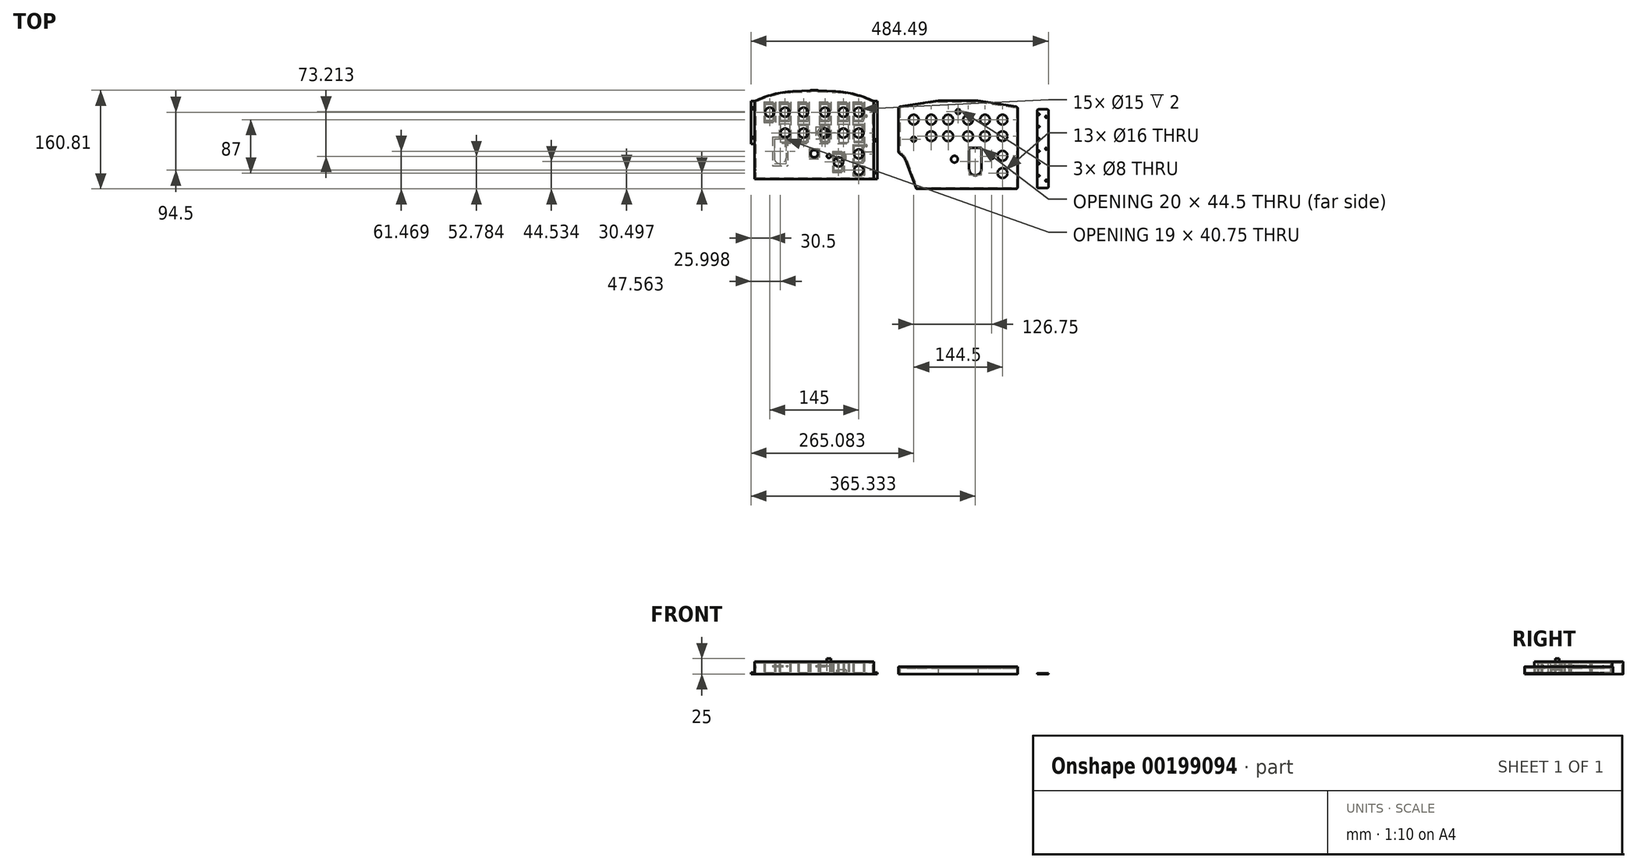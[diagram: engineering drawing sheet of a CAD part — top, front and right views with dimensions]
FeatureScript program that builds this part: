
annotation { "Feature Type Name" : "Feature", "Feature Type Description" : "" }
export const myFeature = defineFeature(function(context is Context, id is Id, definition is map)
    precondition{}
    {
        {
            var Q0;
            Q0=qCreatedBy(makeId("Top.planeOp"),FACE);
            var sketch = newSketch(context, id + "F0", { "sketchPlane" : qUnion([Q0])});
            skLineSegment(sketch, "E0.bottom", {"start": v(-74, 30.66) * mm, "end": v(-59, 30.66) * mm});
            skLineSegment(sketch, "E0.top", {"start": v(-74, 0.66) * mm, "end": v(-59, 0.66) * mm});
            skLineSegment(sketch, "E0.left", {"start": v(-74, 30.66) * mm, "end": v(-74, 0.66) * mm});
            skLineSegment(sketch, "E0.right", {"start": v(-59, 30.66) * mm, "end": v(-59, 0.66) * mm});
            skLineSegment(sketch, "E1.bottom", {"start": v(-49, 30.66) * mm, "end": v(-34, 30.66) * mm});
            skLineSegment(sketch, "E1.top", {"start": v(-49, 0.66) * mm, "end": v(-34, 0.66) * mm});
            skLineSegment(sketch, "E1.left", {"start": v(-49, 30.66) * mm, "end": v(-49, 0.66) * mm});
            skLineSegment(sketch, "E1.right", {"start": v(-34, 30.66) * mm, "end": v(-34, 0.66) * mm});
            skLineSegment(sketch, "E2.bottom", {"start": v(-19, 30.66) * mm, "end": v(-4, 30.66) * mm});
            skLineSegment(sketch, "E2.top", {"start": v(-19, 0.66) * mm, "end": v(-4, 0.66) * mm});
            skLineSegment(sketch, "E2.left", {"start": v(-19, 30.66) * mm, "end": v(-19, 0.66) * mm});
            skLineSegment(sketch, "E2.right", {"start": v(-4, 30.66) * mm, "end": v(-4, 0.66) * mm});
            skLineSegment(sketch, "E3.bottom", {"start": v(16, 30.66) * mm, "end": v(31, 30.66) * mm});
            skLineSegment(sketch, "E3.top", {"start": v(16, 0.66) * mm, "end": v(31, 0.66) * mm});
            skLineSegment(sketch, "E3.left", {"start": v(16, 30.66) * mm, "end": v(16, 0.66) * mm});
            skLineSegment(sketch, "E3.right", {"start": v(31, 30.66) * mm, "end": v(31, 0.66) * mm});
            skLineSegment(sketch, "E4.bottom", {"start": v(46, 30.66) * mm, "end": v(61, 30.66) * mm});
            skLineSegment(sketch, "E4.top", {"start": v(46, 0.66) * mm, "end": v(61, 0.66) * mm});
            skLineSegment(sketch, "E4.left", {"start": v(46, 30.66) * mm, "end": v(46, 0.66) * mm});
            skLineSegment(sketch, "E4.right", {"start": v(61, 30.66) * mm, "end": v(61, 0.66) * mm});
            skLineSegment(sketch, "E5.bottom", {"start": v(71, 30.66) * mm, "end": v(86, 30.66) * mm});
            skLineSegment(sketch, "E5.top", {"start": v(71, 0.66) * mm, "end": v(86, 0.66) * mm});
            skLineSegment(sketch, "E5.left", {"start": v(71, 30.66) * mm, "end": v(71, 0.66) * mm});
            skLineSegment(sketch, "E5.right", {"start": v(86, 30.66) * mm, "end": v(86, 0.66) * mm});
            skLineSegment(sketch, "E6.bottom", {"start": v(-19, -3.34) * mm, "end": v(-4, -3.34) * mm});
            skLineSegment(sketch, "E6.top", {"start": v(-19, -33.34) * mm, "end": v(-4, -33.34) * mm});
            skLineSegment(sketch, "E6.left", {"start": v(-19, -3.34) * mm, "end": v(-19, -33.34) * mm});
            skLineSegment(sketch, "E6.right", {"start": v(-4, -3.34) * mm, "end": v(-4, -33.34) * mm});
            skLineSegment(sketch, "E7.bottom", {"start": v(16, -3.34) * mm, "end": v(31, -3.34) * mm});
            skLineSegment(sketch, "E7.top", {"start": v(16, -33.34) * mm, "end": v(31, -33.34) * mm});
            skLineSegment(sketch, "E7.left", {"start": v(16, -3.34) * mm, "end": v(16, -33.34) * mm});
            skLineSegment(sketch, "E7.right", {"start": v(31, -3.34) * mm, "end": v(31, -33.34) * mm});
            skLineSegment(sketch, "E8.bottom", {"start": v(46, -3.34) * mm, "end": v(61, -3.34) * mm});
            skLineSegment(sketch, "E8.top", {"start": v(46, -33.34) * mm, "end": v(61, -33.34) * mm});
            skLineSegment(sketch, "E8.left", {"start": v(46, -3.34) * mm, "end": v(46, -33.34) * mm});
            skLineSegment(sketch, "E8.right", {"start": v(61, -3.34) * mm, "end": v(61, -33.34) * mm});
            skLineSegment(sketch, "E9.bottom", {"start": v(71, -3.34) * mm, "end": v(86, -3.34) * mm});
            skLineSegment(sketch, "E9.top", {"start": v(71, -33.34) * mm, "end": v(86, -33.34) * mm});
            skLineSegment(sketch, "E9.left", {"start": v(71, -3.34) * mm, "end": v(71, -33.34) * mm});
            skLineSegment(sketch, "E9.right", {"start": v(86, -3.34) * mm, "end": v(86, -33.34) * mm});
            skLineSegment(sketch, "E10.bottom", {"start": v(71, -37.34) * mm, "end": v(86, -37.34) * mm});
            skLineSegment(sketch, "E10.top", {"start": v(71, -67.34) * mm, "end": v(86, -67.34) * mm});
            skLineSegment(sketch, "E10.left", {"start": v(71, -37.34) * mm, "end": v(71, -67.34) * mm});
            skLineSegment(sketch, "E10.right", {"start": v(86, -37.34) * mm, "end": v(86, -67.34) * mm});
            skLineSegment(sketch, "E11.bottom", {"start": v(-34, -3.34) * mm, "end": v(-49, -3.34) * mm});
            skLineSegment(sketch, "E11.top", {"start": v(-34, -33.34) * mm, "end": v(-49, -33.34) * mm});
            skLineSegment(sketch, "E11.left", {"start": v(-34, -3.34) * mm, "end": v(-34, -33.34) * mm});
            skLineSegment(sketch, "E11.right", {"start": v(-49, -3.34) * mm, "end": v(-49, -33.34) * mm});
            skLineSegment(sketch, "E12.bottom", {"start": v(0, -45.34) * mm, "end": v(12, -45.34) * mm});
            skLineSegment(sketch, "E12.top", {"start": v(0, -58.34) * mm, "end": v(12, -58.34) * mm});
            skLineSegment(sketch, "E12.left", {"start": v(0, -45.34) * mm, "end": v(0, -58.34) * mm});
            skLineSegment(sketch, "E12.right", {"start": v(12, -45.34) * mm, "end": v(12, -58.34) * mm});
            skLineSegment(sketch, "E13.bottom", {"start": v(38, -50.34) * mm, "end": v(53, -50.34) * mm});
            skLineSegment(sketch, "E13.top", {"start": v(38, -80.34) * mm, "end": v(53, -80.34) * mm});
            skLineSegment(sketch, "E13.left", {"start": v(38, -50.34) * mm, "end": v(38, -80.34) * mm});
            skLineSegment(sketch, "E13.right", {"start": v(53, -50.34) * mm, "end": v(53, -80.34) * mm});
            skLineSegment(sketch, "E14.bottom", {"start": v(71, -71.34) * mm, "end": v(86, -71.34) * mm});
            skLineSegment(sketch, "E14.top", {"start": v(71, -86.34) * mm, "end": v(86, -86.34) * mm});
            skLineSegment(sketch, "E14.left", {"start": v(71, -71.34) * mm, "end": v(71, -86.34) * mm});
            skLineSegment(sketch, "E14.right", {"start": v(86, -71.34) * mm, "end": v(86, -86.34) * mm});
            skLineSegment(sketch, "E15.bottom", {"start": v(-89, 33.66) * mm, "end": v(101, 33.66) * mm});
            skLineSegment(sketch, "E15.top", {"start": v(-89, -91.34) * mm, "end": v(101, -91.34) * mm});
            skLineSegment(sketch, "E15.left", {"start": v(-89, 33.66) * mm, "end": v(-89, -91.34) * mm});
            skLineSegment(sketch, "E15.right", {"start": v(101, 33.66) * mm, "end": v(101, -91.34) * mm});
            skSolve(sketch);
        }
        {
            var Q0;
            Q0=makeQuery(id+"F0.imprint","IMPRINT",FACE,{"disambiguationData":[TD([[makeQuery(id+"F0.imprint","IMPRINT",EDGE,{"derivedFrom":sQuery(id+"F0.wireOp",EDGE,"E0.bottom")}),1.0]])]});
            extrude(context, id + "F1", {"entities" : qUnion([Q0]), "depth" : 18 * mm});
        }
        {
            var Q0;
            Q0=makeQuery(id+"F1.opExtrude","CAP_FACE",FACE,{"disambiguationData":[OSD([sQuery(id+"F0.wireOp",EDGE,"E0.bottom"),sQuery(id+"F0.wireOp",EDGE,"E0.top"),sQuery(id+"F0.wireOp",EDGE,"E0.left"),sQuery(id+"F0.wireOp",EDGE,"E0.right"),sQuery(id+"F0.wireOp",EDGE,"E1.bottom"),sQuery(id+"F0.wireOp",EDGE,"E1.top"),sQuery(id+"F0.wireOp",EDGE,"E1.left"),sQuery(id+"F0.wireOp",EDGE,"E1.right"),sQuery(id+"F0.wireOp",EDGE,"E2.bottom"),sQuery(id+"F0.wireOp",EDGE,"E2.top"),sQuery(id+"F0.wireOp",EDGE,"E2.left"),sQuery(id+"F0.wireOp",EDGE,"E2.right"),sQuery(id+"F0.wireOp",EDGE,"E3.bottom"),sQuery(id+"F0.wireOp",EDGE,"E3.top"),sQuery(id+"F0.wireOp",EDGE,"E3.left"),sQuery(id+"F0.wireOp",EDGE,"E3.right"),sQuery(id+"F0.wireOp",EDGE,"E4.bottom"),sQuery(id+"F0.wireOp",EDGE,"E4.top"),sQuery(id+"F0.wireOp",EDGE,"E4.left"),sQuery(id+"F0.wireOp",EDGE,"E4.right"),sQuery(id+"F0.wireOp",EDGE,"E5.bottom"),sQuery(id+"F0.wireOp",EDGE,"E5.top"),sQuery(id+"F0.wireOp",EDGE,"E5.left"),sQuery(id+"F0.wireOp",EDGE,"E5.right"),sQuery(id+"F0.wireOp",EDGE,"E6.bottom"),sQuery(id+"F0.wireOp",EDGE,"E6.top"),sQuery(id+"F0.wireOp",EDGE,"E6.left"),sQuery(id+"F0.wireOp",EDGE,"E6.right"),sQuery(id+"F0.wireOp",EDGE,"E7.bottom"),sQuery(id+"F0.wireOp",EDGE,"E7.top"),sQuery(id+"F0.wireOp",EDGE,"E7.left"),sQuery(id+"F0.wireOp",EDGE,"E7.right"),sQuery(id+"F0.wireOp",EDGE,"E8.bottom"),sQuery(id+"F0.wireOp",EDGE,"E8.top"),sQuery(id+"F0.wireOp",EDGE,"E8.left"),sQuery(id+"F0.wireOp",EDGE,"E8.right"),sQuery(id+"F0.wireOp",EDGE,"E9.bottom"),sQuery(id+"F0.wireOp",EDGE,"E9.top"),sQuery(id+"F0.wireOp",EDGE,"E9.left"),sQuery(id+"F0.wireOp",EDGE,"E9.right"),sQuery(id+"F0.wireOp",EDGE,"E10.bottom"),sQuery(id+"F0.wireOp",EDGE,"E10.top"),sQuery(id+"F0.wireOp",EDGE,"E10.left"),sQuery(id+"F0.wireOp",EDGE,"E10.right"),sQuery(id+"F0.wireOp",EDGE,"E11.bottom"),sQuery(id+"F0.wireOp",EDGE,"E11.top"),sQuery(id+"F0.wireOp",EDGE,"E11.left"),sQuery(id+"F0.wireOp",EDGE,"E11.right"),sQuery(id+"F0.wireOp",EDGE,"E12.bottom"),sQuery(id+"F0.wireOp",EDGE,"E12.top"),sQuery(id+"F0.wireOp",EDGE,"E12.left"),sQuery(id+"F0.wireOp",EDGE,"E12.right"),sQuery(id+"F0.wireOp",EDGE,"E13.bottom"),sQuery(id+"F0.wireOp",EDGE,"E13.top"),sQuery(id+"F0.wireOp",EDGE,"E13.left"),sQuery(id+"F0.wireOp",EDGE,"E13.right"),sQuery(id+"F0.wireOp",EDGE,"E14.bottom"),sQuery(id+"F0.wireOp",EDGE,"E14.top"),sQuery(id+"F0.wireOp",EDGE,"E14.left"),sQuery(id+"F0.wireOp",EDGE,"E14.right"),sQuery(id+"F0.wireOp",EDGE,"E15.bottom"),sQuery(id+"F0.wireOp",EDGE,"E15.top"),sQuery(id+"F0.wireOp",EDGE,"E15.left"),sQuery(id+"F0.wireOp",EDGE,"E15.right")])],"isStart":false});
            var sketch = newSketch(context, id + "F2", { "sketchPlane" : qUnion([Q0])});
            skLineSegment(sketch, "E16.bottom", {"start": v(-89, 33.66) * mm, "end": v(101, 33.66) * mm});
            skLineSegment(sketch, "E16.top", {"start": v(-89, -91.34) * mm, "end": v(101, -91.34) * mm});
            skLineSegment(sketch, "E16.left", {"start": v(-89, 33.66) * mm, "end": v(-89, -91.34) * mm});
            skLineSegment(sketch, "E16.right", {"start": v(101, 33.66) * mm, "end": v(101, -91.34) * mm});
            skCircle(sketch, "E17", {"center": v(-66.5, 15.66) * mm, "radius": 7.5 * mm});
            skPoint(sketch, "E18", {"position": v(-66.5, 30.66) * mm});
            skCircle(sketch, "E19", {"center": v(-41.5, 15.66) * mm, "radius": 7.5 * mm});
            skPoint(sketch, "E19.centerSnap0", {"position": v(-41.5, 30.66) * mm});
            skCircle(sketch, "E20", {"center": v(-11.5, 15.66) * mm, "radius": 7.5 * mm});
            skPoint(sketch, "E20.centerSnap0", {"position": v(-11.5, 30.66) * mm});
            skPoint(sketch, "E20.centerSnap1", {"position": v(-34, 15.66) * mm});
            skCircle(sketch, "E21", {"center": v(23.5, 15.66) * mm, "radius": 7.5 * mm});
            skPoint(sketch, "E21.centerSnap0", {"position": v(23.5, 30.66) * mm});
            skCircle(sketch, "E22", {"center": v(53.5, 15.66) * mm, "radius": 7.5 * mm});
            skPoint(sketch, "E22.centerSnap0", {"position": v(53.5, 30.66) * mm});
            skPoint(sketch, "E22.centerSnap1", {"position": v(31, 15.66) * mm});
            skCircle(sketch, "E23", {"center": v(78.5, 15.66) * mm, "radius": 7.5 * mm});
            skPoint(sketch, "E23.centerSnap0", {"position": v(78.5, 30.66) * mm});
            skCircle(sketch, "E24", {"center": v(-11.5, -18.34) * mm, "radius": 7.5 * mm});
            skCircle(sketch, "E25", {"center": v(23.5, -18.34) * mm, "radius": 7.5 * mm});
            skPoint(sketch, "E25.centerSnap0", {"position": v(23.5, -3.34) * mm});
            skPoint(sketch, "E25.centerSnap1", {"position": v(-4, -18.34) * mm});
            skCircle(sketch, "E26", {"center": v(53.5, -18.34) * mm, "radius": 7.5 * mm});
            skPoint(sketch, "E26.centerSnap0", {"position": v(53.5, -3.34) * mm});
            skPoint(sketch, "E26.centerSnap1", {"position": v(31, -18.34) * mm});
            skCircle(sketch, "E27", {"center": v(78.5, -18.34) * mm, "radius": 7.5 * mm});
            skPoint(sketch, "E27.centerSnap0", {"position": v(78.5, -3.34) * mm});
            skCircle(sketch, "E28", {"center": v(45.5, -65.34) * mm, "radius": 7.5 * mm});
            skPoint(sketch, "E28.centerSnap0", {"position": v(45.5, -50.34) * mm});
            skCircle(sketch, "E29", {"center": v(78.5, -52.34) * mm, "radius": 7.5 * mm});
            skPoint(sketch, "E29.centerSnap0", {"position": v(78.5, -37.34) * mm});
            skCircle(sketch, "E30", {"center": v(-41.5, -18.34) * mm, "radius": 7.5 * mm});
            skPoint(sketch, "E30.centerSnap0", {"position": v(-41.5, -3.34) * mm});
            skCircle(sketch, "E31", {"center": v(78.5, -78.84) * mm, "radius": 7.5 * mm});
            skPoint(sketch, "E31.centerSnap0", {"position": v(86, -78.84) * mm});
            skCircle(sketch, "E32", {"center": v(6, -51.84) * mm, "radius": 6 * mm});
            skPoint(sketch, "E32.centerSnap0", {"position": v(0, -51.84) * mm});
            skPoint(sketch, "E32.centerSnap1", {"position": v(6, -45.34) * mm});
            skSolve(sketch);
        }
        {
            var Q0;
            Q0=qSketchRegion(id+"F2",true);
            extrude(context, id + "F3", {"entities" : qUnion([Q0]), "depth" : 2 * mm});
        }
        {
            var Q0;
            Q0=makeQuery(id+"F3.opExtrude","CAP_FACE",FACE,{"disambiguationData":[OSD([sQuery(id+"F2.wireOp",EDGE,"E16.bottom"),sQuery(id+"F2.wireOp",EDGE,"E16.top"),sQuery(id+"F2.wireOp",EDGE,"E16.left"),sQuery(id+"F2.wireOp",EDGE,"E16.right"),sQuery(id+"F2.wireOp",EDGE,"E17"),sQuery(id+"F2.wireOp",EDGE,"E19"),sQuery(id+"F2.wireOp",EDGE,"E20"),sQuery(id+"F2.wireOp",EDGE,"E21"),sQuery(id+"F2.wireOp",EDGE,"E22"),sQuery(id+"F2.wireOp",EDGE,"E23"),sQuery(id+"F2.wireOp",EDGE,"E24"),sQuery(id+"F2.wireOp",EDGE,"E25"),sQuery(id+"F2.wireOp",EDGE,"E26"),sQuery(id+"F2.wireOp",EDGE,"E27"),sQuery(id+"F2.wireOp",EDGE,"E28"),sQuery(id+"F2.wireOp",EDGE,"E29"),sQuery(id+"F2.wireOp",EDGE,"E30"),sQuery(id+"F2.wireOp",EDGE,"E31"),sQuery(id+"F2.wireOp",EDGE,"E32")])],"isStart":false});
            var sketch = newSketch(context, id + "F4", { "sketchPlane" : qUnion([Q0])});
            skLineSegment(sketch, "E33.bottom", {"start": v(-89, 33.66) * mm, "end": v(-91, 33.66) * mm});
            skLineSegment(sketch, "E33.top", {"start": v(-89, -91.34) * mm, "end": v(-91, -91.34) * mm});
            skLineSegment(sketch, "E33.left", {"start": v(-89, 33.66) * mm, "end": v(-89, -91.34) * mm});
            skLineSegment(sketch, "E33.right", {"start": v(-91, 33.66) * mm, "end": v(-91, -91.34) * mm});
            skLineSegment(sketch, "E34.bottom", {"start": v(101, 33.66) * mm, "end": v(103, 33.66) * mm});
            skLineSegment(sketch, "E34.top", {"start": v(101, -91.34) * mm, "end": v(103, -91.34) * mm});
            skLineSegment(sketch, "E34.left", {"start": v(101, 33.66) * mm, "end": v(101, -91.34) * mm});
            skLineSegment(sketch, "E34.right", {"start": v(103, 33.66) * mm, "end": v(103, -91.34) * mm});
            skLineSegment(sketch, "E35.bottom", {"start": v(-91, -91.34) * mm, "end": v(103, -91.34) * mm});
            skLineSegment(sketch, "E35.top", {"start": v(-91, -93.34) * mm, "end": v(103, -93.34) * mm});
            skLineSegment(sketch, "E35.left", {"start": v(-91, -91.34) * mm, "end": v(-91, -93.34) * mm});
            skLineSegment(sketch, "E35.right", {"start": v(103, -91.34) * mm, "end": v(103, -93.34) * mm});
            skLineSegment(sketch, "E36", {"start": v(-29, 49.65) * mm, "end": v(-29, 33.66) * mm});
            skLineSegment(sketch, "E37", {"start": v(41, 49.65) * mm, "end": v(41, 33.66) * mm});
            skPoint(sketch, "E38.orphan", {"position": v(103, 49.4) * mm});
            skLineSegment(sketch, "E39", {"start": v(-29, 49.65) * mm, "end": v(6, 51.66) * mm});
            skLineSegment(sketch, "E40", {"start": v(6, 51.66) * mm, "end": v(41, 49.65) * mm});
            skArc(sketch, "E41", {"start": v(-29, 49.65) * mm, "mid": v(-60.78, 44.7) * mm, "end": v(-91, 33.66) * mm});
            skArc(sketch, "E42", {"start": v(103, 33.66) * mm, "mid": v(72.78, 44.7) * mm, "end": v(41, 49.65) * mm});
            skLineSegment(sketch, "E43.bottom", {"start": v(-89, 33.66) * mm, "end": v(101, 33.66) * mm});
            skLineSegment(sketch, "E43.top", {"start": v(-89, -91.34) * mm, "end": v(101, -91.34) * mm});
            skSolve(sketch);
        }
        {
            var Q0;
            Q0=qSketchRegion(id+"F4",true);
            extrude(context, id + "F5", {"entities" : qUnion([Q0]), "operationType" : NewBodyOperationType.ADD, "oppositeDirection" : true, "depth" : 20 * mm});
        }
        {
            var Q0;
            Q0=makeQuery(id+"F5.opExtrude","SWEPT_EDGE",EDGE,{"disambiguationData":[OSD([sQuery(id+"F4.wireOp",EDGE,"E39"),sQuery(id+"F4.wireOp",EDGE,"E40")])]});
            fillet(context, id + "F6", {"entities" : qUnion([Q0]), "radius" : 115.17 * mm, "tangentPropagation" : true, "allowEdgeOverflow" : false});
        }
        {
            var Q0;
            Q0=makeQuery(id+"F5.opExtrude","CAP_FACE",FACE,{"disambiguationData":[OSD([sQuery(id+"F4.wireOp",EDGE,"E33.right"),sQuery(id+"F4.wireOp",EDGE,"E34.right"),sQuery(id+"F4.wireOp",EDGE,"E35.top"),sQuery(id+"F4.wireOp",EDGE,"E35.left"),sQuery(id+"F4.wireOp",EDGE,"E35.right"),sQuery(id+"F4.wireOp",EDGE,"E39"),sQuery(id+"F4.wireOp",EDGE,"E40"),sQuery(id+"F4.wireOp",EDGE,"E41"),sQuery(id+"F4.wireOp",EDGE,"E42")])],"isStart":false});
            shell(context, id + "F7", {"entities" : qUnion([Q0]), "thickness" : 2 * mm});
        }
        {
            var Q0;
            Q0=makeQuery(id+"F1.opExtrude","CAP_FACE",FACE,{"disambiguationData":[OSD([sQuery(id+"F0.wireOp",EDGE,"E0.bottom"),sQuery(id+"F0.wireOp",EDGE,"E0.top"),sQuery(id+"F0.wireOp",EDGE,"E0.left"),sQuery(id+"F0.wireOp",EDGE,"E0.right"),sQuery(id+"F0.wireOp",EDGE,"E1.bottom"),sQuery(id+"F0.wireOp",EDGE,"E1.top"),sQuery(id+"F0.wireOp",EDGE,"E1.left"),sQuery(id+"F0.wireOp",EDGE,"E1.right"),sQuery(id+"F0.wireOp",EDGE,"E2.bottom"),sQuery(id+"F0.wireOp",EDGE,"E2.top"),sQuery(id+"F0.wireOp",EDGE,"E2.left"),sQuery(id+"F0.wireOp",EDGE,"E2.right"),sQuery(id+"F0.wireOp",EDGE,"E3.bottom"),sQuery(id+"F0.wireOp",EDGE,"E3.top"),sQuery(id+"F0.wireOp",EDGE,"E3.left"),sQuery(id+"F0.wireOp",EDGE,"E3.right"),sQuery(id+"F0.wireOp",EDGE,"E4.bottom"),sQuery(id+"F0.wireOp",EDGE,"E4.top"),sQuery(id+"F0.wireOp",EDGE,"E4.left"),sQuery(id+"F0.wireOp",EDGE,"E4.right"),sQuery(id+"F0.wireOp",EDGE,"E5.bottom"),sQuery(id+"F0.wireOp",EDGE,"E5.top"),sQuery(id+"F0.wireOp",EDGE,"E5.left"),sQuery(id+"F0.wireOp",EDGE,"E5.right"),sQuery(id+"F0.wireOp",EDGE,"E6.bottom"),sQuery(id+"F0.wireOp",EDGE,"E6.top"),sQuery(id+"F0.wireOp",EDGE,"E6.left"),sQuery(id+"F0.wireOp",EDGE,"E6.right"),sQuery(id+"F0.wireOp",EDGE,"E7.bottom"),sQuery(id+"F0.wireOp",EDGE,"E7.top"),sQuery(id+"F0.wireOp",EDGE,"E7.left"),sQuery(id+"F0.wireOp",EDGE,"E7.right"),sQuery(id+"F0.wireOp",EDGE,"E8.bottom"),sQuery(id+"F0.wireOp",EDGE,"E8.top"),sQuery(id+"F0.wireOp",EDGE,"E8.left"),sQuery(id+"F0.wireOp",EDGE,"E8.right"),sQuery(id+"F0.wireOp",EDGE,"E9.bottom"),sQuery(id+"F0.wireOp",EDGE,"E9.top"),sQuery(id+"F0.wireOp",EDGE,"E9.left"),sQuery(id+"F0.wireOp",EDGE,"E9.right"),sQuery(id+"F0.wireOp",EDGE,"E10.bottom"),sQuery(id+"F0.wireOp",EDGE,"E10.top"),sQuery(id+"F0.wireOp",EDGE,"E10.left"),sQuery(id+"F0.wireOp",EDGE,"E10.right"),sQuery(id+"F0.wireOp",EDGE,"E11.bottom"),sQuery(id+"F0.wireOp",EDGE,"E11.top"),sQuery(id+"F0.wireOp",EDGE,"E11.left"),sQuery(id+"F0.wireOp",EDGE,"E11.right"),sQuery(id+"F0.wireOp",EDGE,"E12.bottom"),sQuery(id+"F0.wireOp",EDGE,"E12.top"),sQuery(id+"F0.wireOp",EDGE,"E12.left"),sQuery(id+"F0.wireOp",EDGE,"E12.right"),sQuery(id+"F0.wireOp",EDGE,"E13.bottom"),sQuery(id+"F0.wireOp",EDGE,"E13.top"),sQuery(id+"F0.wireOp",EDGE,"E13.left"),sQuery(id+"F0.wireOp",EDGE,"E13.right"),sQuery(id+"F0.wireOp",EDGE,"E14.bottom"),sQuery(id+"F0.wireOp",EDGE,"E14.top"),sQuery(id+"F0.wireOp",EDGE,"E14.left"),sQuery(id+"F0.wireOp",EDGE,"E14.right"),sQuery(id+"F0.wireOp",EDGE,"E15.bottom"),sQuery(id+"F0.wireOp",EDGE,"E15.top"),sQuery(id+"F0.wireOp",EDGE,"E15.left"),sQuery(id+"F0.wireOp",EDGE,"E15.right")])],"isStart":true});
            var sketch = newSketch(context, id + "F8", { "sketchPlane" : qUnion([Q0])});
            skLineSegment(sketch, "E44.bottom", {"start": v(-97, -34.16) * mm, "end": v(-91, -34.16) * mm});
            skLineSegment(sketch, "E44.top", {"start": v(-97, 35.84) * mm, "end": v(-91, 35.84) * mm});
            skLineSegment(sketch, "E44.left", {"start": v(-97, -34.16) * mm, "end": v(-97, 35.84) * mm});
            skLineSegment(sketch, "E44.right", {"start": v(-91, -34.16) * mm, "end": v(-91, 35.84) * mm});
            skLineSegment(sketch, "E45.bottom", {"start": v(103, -33.66) * mm, "end": v(109, -33.66) * mm});
            skLineSegment(sketch, "E45.top", {"start": v(103, 93.34) * mm, "end": v(109, 93.34) * mm});
            skLineSegment(sketch, "E45.left", {"start": v(103, -33.66) * mm, "end": v(103, 93.34) * mm});
            skLineSegment(sketch, "E45.right", {"start": v(109, -33.66) * mm, "end": v(109, 93.34) * mm});
            skCircle(sketch, "E46", {"center": v(-94, -22.16) * mm, "radius": 1.5 * mm});
            skCircle(sketch, "E47", {"center": v(-94, 25.84) * mm, "radius": 1.5 * mm});
            skCircle(sketch, "E48", {"center": v(106, -22.16) * mm, "radius": 1.5 * mm});
            skCircle(sketch, "E49", {"center": v(106, 29.84) * mm, "radius": 1.5 * mm});
            skCircle(sketch, "E50", {"center": v(106, 81.84) * mm, "radius": 1.5 * mm});
            skSolve(sketch);
        }
        {
            var Q0;
            Q0=qSketchRegion(id+"F8",true);
            extrude(context, id + "F9", {"entities" : qUnion([Q0]), "operationType" : NewBodyOperationType.ADD, "oppositeDirection" : true, "depth" : 2 * mm});
        }
        {
            var Q0;
            Q0=makeQuery(id+"F5.opExtrude","SWEPT_FACE",FACE,{"disambiguationData":[OSD([sQuery(id+"F4.wireOp",EDGE,"E33.right"),sQuery(id+"F4.wireOp",EDGE,"E35.left")])]});
            var sketch = newSketch(context, id + "F10", { "sketchPlane" : qUnion([Q0])});
            skCircle(sketch, "E51", {"center": v(-18.66, 11) * mm, "radius": 1.5 * mm});
            skCircle(sketch, "E52", {"center": v(78.38, 11) * mm, "radius": 1.5 * mm});
            skCircle(sketch, "E53", {"center": v(29.88, 11) * mm, "radius": 1.5 * mm});
            skSolve(sketch);
        }
        {
            var Q0;
            Q0=qSketchRegion(id+"F10",true);
            extrude(context, id + "F11", {"entities" : qUnion([Q0]), "operationType" : NewBodyOperationType.REMOVE, "oppositeDirection" : true, "depth" : 8 * mm});
        }
        {
            var Q0;
            Q0=makeQuery(id+"F5.opExtrude","SWEPT_FACE",FACE,{"disambiguationData":[OSD([sQuery(id+"F4.wireOp",EDGE,"E34.right"),sQuery(id+"F4.wireOp",EDGE,"E35.right")])]});
            var sketch = newSketch(context, id + "F12", { "sketchPlane" : qUnion([Q0])});
            skCircle(sketch, "E54", {"center": v(-78.34, 11) * mm, "radius": 1.5 * mm});
            skCircle(sketch, "E55", {"center": v(18.66, 11) * mm, "radius": 1.5 * mm});
            skCircle(sketch, "E56", {"center": v(-29.84, 11) * mm, "radius": 1.5 * mm});
            skSolve(sketch);
        }
        {
            var Q0;
            Q0=qSketchRegion(id+"F12",true);
            extrude(context, id + "F13", {"entities" : qUnion([Q0]), "operationType" : NewBodyOperationType.REMOVE, "oppositeDirection" : true, "depth" : 8 * mm});
        }
        {
            var Q0;
            Q0=makeQuery(id+"F1.opExtrude","CAP_FACE",FACE,{"disambiguationData":[OSD([sQuery(id+"F0.wireOp",EDGE,"E0.bottom"),sQuery(id+"F0.wireOp",EDGE,"E0.top"),sQuery(id+"F0.wireOp",EDGE,"E0.left"),sQuery(id+"F0.wireOp",EDGE,"E0.right"),sQuery(id+"F0.wireOp",EDGE,"E1.bottom"),sQuery(id+"F0.wireOp",EDGE,"E1.top"),sQuery(id+"F0.wireOp",EDGE,"E1.left"),sQuery(id+"F0.wireOp",EDGE,"E1.right"),sQuery(id+"F0.wireOp",EDGE,"E2.bottom"),sQuery(id+"F0.wireOp",EDGE,"E2.top"),sQuery(id+"F0.wireOp",EDGE,"E2.left"),sQuery(id+"F0.wireOp",EDGE,"E2.right"),sQuery(id+"F0.wireOp",EDGE,"E3.bottom"),sQuery(id+"F0.wireOp",EDGE,"E3.top"),sQuery(id+"F0.wireOp",EDGE,"E3.left"),sQuery(id+"F0.wireOp",EDGE,"E3.right"),sQuery(id+"F0.wireOp",EDGE,"E4.bottom"),sQuery(id+"F0.wireOp",EDGE,"E4.top"),sQuery(id+"F0.wireOp",EDGE,"E4.left"),sQuery(id+"F0.wireOp",EDGE,"E4.right"),sQuery(id+"F0.wireOp",EDGE,"E5.bottom"),sQuery(id+"F0.wireOp",EDGE,"E5.top"),sQuery(id+"F0.wireOp",EDGE,"E5.left"),sQuery(id+"F0.wireOp",EDGE,"E5.right"),sQuery(id+"F0.wireOp",EDGE,"E6.bottom"),sQuery(id+"F0.wireOp",EDGE,"E6.top"),sQuery(id+"F0.wireOp",EDGE,"E6.left"),sQuery(id+"F0.wireOp",EDGE,"E6.right"),sQuery(id+"F0.wireOp",EDGE,"E7.bottom"),sQuery(id+"F0.wireOp",EDGE,"E7.top"),sQuery(id+"F0.wireOp",EDGE,"E7.left"),sQuery(id+"F0.wireOp",EDGE,"E7.right"),sQuery(id+"F0.wireOp",EDGE,"E8.bottom"),sQuery(id+"F0.wireOp",EDGE,"E8.top"),sQuery(id+"F0.wireOp",EDGE,"E8.left"),sQuery(id+"F0.wireOp",EDGE,"E8.right"),sQuery(id+"F0.wireOp",EDGE,"E9.bottom"),sQuery(id+"F0.wireOp",EDGE,"E9.top"),sQuery(id+"F0.wireOp",EDGE,"E9.left"),sQuery(id+"F0.wireOp",EDGE,"E9.right"),sQuery(id+"F0.wireOp",EDGE,"E10.bottom"),sQuery(id+"F0.wireOp",EDGE,"E10.top"),sQuery(id+"F0.wireOp",EDGE,"E10.left"),sQuery(id+"F0.wireOp",EDGE,"E10.right"),sQuery(id+"F0.wireOp",EDGE,"E11.bottom"),sQuery(id+"F0.wireOp",EDGE,"E11.top"),sQuery(id+"F0.wireOp",EDGE,"E11.left"),sQuery(id+"F0.wireOp",EDGE,"E11.right"),sQuery(id+"F0.wireOp",EDGE,"E12.bottom"),sQuery(id+"F0.wireOp",EDGE,"E12.top"),sQuery(id+"F0.wireOp",EDGE,"E12.left"),sQuery(id+"F0.wireOp",EDGE,"E12.right"),sQuery(id+"F0.wireOp",EDGE,"E13.bottom"),sQuery(id+"F0.wireOp",EDGE,"E13.top"),sQuery(id+"F0.wireOp",EDGE,"E13.left"),sQuery(id+"F0.wireOp",EDGE,"E13.right"),sQuery(id+"F0.wireOp",EDGE,"E14.bottom"),sQuery(id+"F0.wireOp",EDGE,"E14.top"),sQuery(id+"F0.wireOp",EDGE,"E14.left"),sQuery(id+"F0.wireOp",EDGE,"E14.right"),sQuery(id+"F0.wireOp",EDGE,"E15.bottom"),sQuery(id+"F0.wireOp",EDGE,"E15.top"),sQuery(id+"F0.wireOp",EDGE,"E15.left"),sQuery(id+"F0.wireOp",EDGE,"E15.right")])],"isStart":true});
            var sketch = newSketch(context, id + "F14", { "sketchPlane" : qUnion([Q0])});
            skLineSegment(sketch, "E57.bottom", {"start": v(-19, -2.66) * mm, "end": v(-6, -2.66) * mm});
            skLineSegment(sketch, "E57.top", {"start": v(-19, -28.66) * mm, "end": v(-6, -28.66) * mm});
            skLineSegment(sketch, "E57.left", {"start": v(-19, -2.66) * mm, "end": v(-19, -28.66) * mm});
            skLineSegment(sketch, "E57.right", {"start": v(-6, -2.66) * mm, "end": v(-6, -28.66) * mm});
            skLineSegment(sketch, "E58.bottom", {"start": v(-49, -2.66) * mm, "end": v(-36, -2.66) * mm});
            skLineSegment(sketch, "E58.top", {"start": v(-49, -28.66) * mm, "end": v(-36, -28.66) * mm});
            skLineSegment(sketch, "E58.left", {"start": v(-49, -2.66) * mm, "end": v(-49, -28.66) * mm});
            skLineSegment(sketch, "E58.right", {"start": v(-36, -2.66) * mm, "end": v(-36, -28.66) * mm});
            skLineSegment(sketch, "E59.bottom", {"start": v(-74, -2.66) * mm, "end": v(-61, -2.66) * mm});
            skLineSegment(sketch, "E59.top", {"start": v(-74, -28.66) * mm, "end": v(-61, -28.66) * mm});
            skLineSegment(sketch, "E59.left", {"start": v(-74, -2.66) * mm, "end": v(-74, -28.66) * mm});
            skLineSegment(sketch, "E59.right", {"start": v(-61, -2.66) * mm, "end": v(-61, -28.66) * mm});
            skLineSegment(sketch, "E60.bottom", {"start": v(16, -2.66) * mm, "end": v(29, -2.66) * mm});
            skLineSegment(sketch, "E60.top", {"start": v(16, -28.66) * mm, "end": v(29, -28.66) * mm});
            skLineSegment(sketch, "E60.left", {"start": v(16, -2.66) * mm, "end": v(16, -28.66) * mm});
            skLineSegment(sketch, "E60.right", {"start": v(29, -2.66) * mm, "end": v(29, -28.66) * mm});
            skLineSegment(sketch, "E61.bottom", {"start": v(46, -2.66) * mm, "end": v(59, -2.66) * mm});
            skLineSegment(sketch, "E61.top", {"start": v(46, -28.66) * mm, "end": v(59, -28.66) * mm});
            skLineSegment(sketch, "E61.left", {"start": v(46, -2.66) * mm, "end": v(46, -28.66) * mm});
            skLineSegment(sketch, "E61.right", {"start": v(59, -2.66) * mm, "end": v(59, -28.66) * mm});
            skLineSegment(sketch, "E62.bottom", {"start": v(71, -2.66) * mm, "end": v(84, -2.66) * mm});
            skLineSegment(sketch, "E62.top", {"start": v(71, -28.66) * mm, "end": v(84, -28.66) * mm});
            skLineSegment(sketch, "E62.left", {"start": v(71, -2.66) * mm, "end": v(71, -28.66) * mm});
            skLineSegment(sketch, "E62.right", {"start": v(84, -2.66) * mm, "end": v(84, -28.66) * mm});
            skLineSegment(sketch, "E63.bottom", {"start": v(-19, 31.34) * mm, "end": v(-6, 31.34) * mm});
            skLineSegment(sketch, "E63.top", {"start": v(-19, 5.34) * mm, "end": v(-6, 5.34) * mm});
            skLineSegment(sketch, "E63.left", {"start": v(-19, 31.34) * mm, "end": v(-19, 5.34) * mm});
            skLineSegment(sketch, "E63.right", {"start": v(-6, 31.34) * mm, "end": v(-6, 5.34) * mm});
            skLineSegment(sketch, "E64.bottom", {"start": v(16, 31.34) * mm, "end": v(29, 31.34) * mm});
            skLineSegment(sketch, "E64.top", {"start": v(16, 5.34) * mm, "end": v(29, 5.34) * mm});
            skLineSegment(sketch, "E64.left", {"start": v(16, 31.34) * mm, "end": v(16, 5.34) * mm});
            skLineSegment(sketch, "E64.right", {"start": v(29, 31.34) * mm, "end": v(29, 5.34) * mm});
            skLineSegment(sketch, "E65.bottom", {"start": v(71, 31.34) * mm, "end": v(84, 31.34) * mm});
            skLineSegment(sketch, "E65.top", {"start": v(71, 5.34) * mm, "end": v(84, 5.34) * mm});
            skLineSegment(sketch, "E65.left", {"start": v(71, 31.34) * mm, "end": v(71, 5.34) * mm});
            skLineSegment(sketch, "E65.right", {"start": v(84, 31.34) * mm, "end": v(84, 5.34) * mm});
            skLineSegment(sketch, "E66.bottom", {"start": v(38, 78.34) * mm, "end": v(51, 78.34) * mm});
            skLineSegment(sketch, "E66.top", {"start": v(38, 52.34) * mm, "end": v(51, 52.34) * mm});
            skLineSegment(sketch, "E66.left", {"start": v(38, 78.34) * mm, "end": v(38, 52.34) * mm});
            skLineSegment(sketch, "E66.right", {"start": v(51, 78.34) * mm, "end": v(51, 52.34) * mm});
            skLineSegment(sketch, "E67.bottom", {"start": v(71, 65.34) * mm, "end": v(84, 65.34) * mm});
            skLineSegment(sketch, "E67.top", {"start": v(71, 39.34) * mm, "end": v(84, 39.34) * mm});
            skLineSegment(sketch, "E67.left", {"start": v(71, 65.34) * mm, "end": v(71, 39.34) * mm});
            skLineSegment(sketch, "E67.right", {"start": v(84, 65.34) * mm, "end": v(84, 39.34) * mm});
            skSolve(sketch);
        }
        {
            var Q0;
            Q0=qSketchRegion(id+"F14",true);
            extrude(context, id + "F15", {"entities" : qUnion([Q0]), "operationType" : NewBodyOperationType.ADD, "oppositeDirection" : true, "depth" : 2 * mm});
        }
        {
            var Q0;
            Q0=qCreatedBy(makeId("Top.planeOp"),FACE);
            var sketch = newSketch(context, id + "F16", { "sketchPlane" : qUnion([Q0])});
            skLineSegment(sketch, "E68.top", {"start": v(174.33, -109.34) * mm, "end": v(334.33, -109.34) * mm});
            skLineSegment(sketch, "E68.left", {"start": v(143.33, 21.7) * mm, "end": v(143.33, -48.57) * mm});
            skLineSegment(sketch, "E68.right", {"start": v(337.33, 21.7) * mm, "end": v(337.33, -106.34) * mm});
            skLineSegment(sketch, "E69", {"start": v(154.92, -63.5) * mm, "end": v(171.53, -107.4) * mm});
            skLineSegment(sketch, "E70", {"start": v(207.83, 34.66) * mm, "end": v(272.83, 34.66) * mm});
            skLineSegment(sketch, "E71", {"start": v(272.83, 34.66) * mm, "end": v(334.81, 24.66) * mm});
            skLineSegment(sketch, "E72", {"start": v(207.83, 34.66) * mm, "end": v(145.85, 24.66) * mm});
            skPoint(sketch, "E73.visualSharp", {"position": v(143.33, 24.25) * mm});
            skArc(sketch, "E73.filletArc", {"start": v(145.85, 24.66) * mm, "mid": v(144.05, 23.64) * mm, "end": v(143.33, 21.7) * mm});
            skPoint(sketch, "E74.visualSharp", {"position": v(337.33, 24.25) * mm});
            skArc(sketch, "E74.filletArc", {"start": v(337.33, 21.7) * mm, "mid": v(336.62, 23.64) * mm, "end": v(334.81, 24.66) * mm});
            skPoint(sketch, "E75.visualSharp", {"position": v(337.33, -109.34) * mm});
            skArc(sketch, "E75.filletArc", {"start": v(334.33, -109.34) * mm, "mid": v(336.45, -108.46) * mm, "end": v(337.33, -106.34) * mm});
            skPoint(sketch, "E76.visualSharp", {"position": v(172.26, -109.34) * mm});
            skArc(sketch, "E76.filletArc", {"start": v(171.53, -107.4) * mm, "mid": v(172.63, -108.8) * mm, "end": v(174.33, -109.34) * mm});
            skArc(sketch, "E77", {"start": v(154.92, -63.5) * mm, "mid": v(150.85, -56.47) * mm, "end": v(144.75, -51.12) * mm});
            skPoint(sketch, "E78.visualSharp", {"position": v(143.33, -50.3) * mm});
            skArc(sketch, "E78.filletArc", {"start": v(143.33, -48.57) * mm, "mid": v(143.7, -50.03) * mm, "end": v(144.75, -51.12) * mm});
            skSolve(sketch);
        }
        {
            var Q0;
            Q0=qSketchRegion(id+"F16",true);
            extrude(context, id + "F17", {"entities" : qUnion([Q0]), "depth" : 11.5 * mm});
        }
        {
            var Q0;
            Q0=makeQuery(id+"F17.opExtrude","CAP_FACE",FACE,{"disambiguationData":[OSD([sQuery(id+"F16.wireOp",EDGE,"E68.top"),sQuery(id+"F16.wireOp",EDGE,"E68.left"),sQuery(id+"F16.wireOp",EDGE,"E68.right"),sQuery(id+"F16.wireOp",EDGE,"E69"),sQuery(id+"F16.wireOp",EDGE,"E70"),sQuery(id+"F16.wireOp",EDGE,"E71"),sQuery(id+"F16.wireOp",EDGE,"E72"),sQuery(id+"F16.wireOp",EDGE,"E73.filletArc"),sQuery(id+"F16.wireOp",EDGE,"E74.filletArc"),sQuery(id+"F16.wireOp",EDGE,"E75.filletArc"),sQuery(id+"F16.wireOp",EDGE,"E76.filletArc"),sQuery(id+"F16.wireOp",EDGE,"E77"),sQuery(id+"F16.wireOp",EDGE,"E78.filletArc")])],"isStart":true});
            shell(context, id + "F18", {"entities" : qUnion([Q0]), "thickness" : 2 * mm});
        }
        {
            var Q0;
            Q0=makeQuery(id+"F17.opExtrude","CAP_FACE",FACE,{"disambiguationData":[OSD([sQuery(id+"F16.wireOp",EDGE,"E68.top"),sQuery(id+"F16.wireOp",EDGE,"E68.left"),sQuery(id+"F16.wireOp",EDGE,"E68.right"),sQuery(id+"F16.wireOp",EDGE,"E69"),sQuery(id+"F16.wireOp",EDGE,"E70"),sQuery(id+"F16.wireOp",EDGE,"E71"),sQuery(id+"F16.wireOp",EDGE,"E72"),sQuery(id+"F16.wireOp",EDGE,"E73.filletArc"),sQuery(id+"F16.wireOp",EDGE,"E74.filletArc"),sQuery(id+"F16.wireOp",EDGE,"E75.filletArc"),sQuery(id+"F16.wireOp",EDGE,"E76.filletArc"),sQuery(id+"F16.wireOp",EDGE,"E77"),sQuery(id+"F16.wireOp",EDGE,"E78.filletArc")])],"isStart":false});
            var sketch = newSketch(context, id + "F19", { "sketchPlane" : qUnion([Q0])});
            skLineSegment(sketch, "E79.bottom", {"start": v(150.33, 21.66) * mm, "end": v(331.33, 21.66) * mm});
            skLineSegment(sketch, "E79.top", {"start": v(185.56, -101.56) * mm, "end": v(331.33, -101.56) * mm});
            skLineSegment(sketch, "E79.left", {"start": v(150.33, 21.66) * mm, "end": v(150.33, -46.56) * mm});
            skLineSegment(sketch, "E79.right", {"start": v(331.33, 21.66) * mm, "end": v(331.33, -101.56) * mm});
            skLineSegment(sketch, "E80", {"start": v(150.33, -46.56) * mm, "end": v(185.56, -46.56) * mm});
            skLineSegment(sketch, "E81", {"start": v(185.56, -46.56) * mm, "end": v(185.56, -101.56) * mm});
            skCircle(sketch, "E82", {"center": v(168.08, 3.66) * mm, "radius": 8 * mm});
            skCircle(sketch, "E83", {"center": v(196.58, 3.66) * mm, "radius": 8 * mm});
            skCircle(sketch, "E84", {"center": v(224.08, 3.66) * mm, "radius": 8 * mm});
            skCircle(sketch, "E85", {"center": v(234.33, -60.84) * mm, "radius": 5.5 * mm});
            skCircle(sketch, "E86", {"center": v(256.58, 3.66) * mm, "radius": 8 * mm});
            skCircle(sketch, "E87", {"center": v(284.08, 3.66) * mm, "radius": 8 * mm});
            skCircle(sketch, "E88", {"center": v(312.58, 3.66) * mm, "radius": 8 * mm});
            skCircle(sketch, "E89", {"center": v(312.58, -55.34) * mm, "radius": 8 * mm});
            skCircle(sketch, "E90", {"center": v(312.58, -83.34) * mm, "radius": 8 * mm});
            skLineSegment(sketch, "E91.top", {"start": v(210.83, 28.66) * mm, "end": v(270.83, 28.66) * mm});
            skLineSegment(sketch, "E91.left", {"start": v(210.83, 21.66) * mm, "end": v(210.83, 28.66) * mm});
            skLineSegment(sketch, "E91.right", {"start": v(270.83, 21.66) * mm, "end": v(270.83, 28.66) * mm});
            skLineSegment(sketch, "E92.left", {"start": v(258.33, -42.56) * mm, "end": v(258.33, -77.06) * mm});
            skLineSegment(sketch, "E92.right", {"start": v(278.33, -42.56) * mm, "end": v(278.33, -77.06) * mm});
            skLineSegment(sketch, "E93", {"start": v(258.33, -42.56) * mm, "end": v(278.33, -42.56) * mm});
            skCircle(sketch, "E94", {"center": v(240.33, 16.66) * mm, "radius": 4 * mm});
            skCircle(sketch, "E95", {"center": v(294.83, -56.56) * mm, "radius": 4 * mm});
            skLineSegment(sketch, "E96.bottom", {"start": v(150.33, 21.66) * mm, "end": v(149.33, 21.66) * mm});
            skLineSegment(sketch, "E96.top", {"start": v(150.33, -46.56) * mm, "end": v(147.33, -46.56) * mm});
            skLineSegment(sketch, "E96.right", {"start": v(147.33, 19.66) * mm, "end": v(147.33, -46.56) * mm});
            skLineSegment(sketch, "E97.bottom", {"start": v(147.33, -46.56) * mm, "end": v(185.56, -46.56) * mm});
            skLineSegment(sketch, "E97.top", {"start": v(149.33, -49.56) * mm, "end": v(185.56, -49.56) * mm});
            skLineSegment(sketch, "E97.left", {"start": v(147.33, -46.56) * mm, "end": v(147.33, -47.56) * mm});
            skLineSegment(sketch, "E97.right", {"start": v(185.56, -46.56) * mm, "end": v(185.56, -49.56) * mm});
            skLineSegment(sketch, "E98.bottom", {"start": v(185.56, -101.56) * mm, "end": v(182.56, -101.56) * mm});
            skLineSegment(sketch, "E98.top", {"start": v(185.56, -49.56) * mm, "end": v(182.56, -49.56) * mm});
            skLineSegment(sketch, "E98.left", {"start": v(185.56, -101.56) * mm, "end": v(185.56, -49.56) * mm});
            skLineSegment(sketch, "E98.right", {"start": v(182.56, -101.56) * mm, "end": v(182.56, -49.56) * mm});
            skLineSegment(sketch, "E99.bottom", {"start": v(182.56, -101.56) * mm, "end": v(254.56, -101.56) * mm});
            skLineSegment(sketch, "E99.top", {"start": v(182.56, -104.56) * mm, "end": v(254.56, -104.56) * mm});
            skLineSegment(sketch, "E99.left", {"start": v(182.56, -101.56) * mm, "end": v(182.56, -104.56) * mm});
            skLineSegment(sketch, "E99.right", {"start": v(254.56, -101.56) * mm, "end": v(254.56, -104.56) * mm});
            skLineSegment(sketch, "E100.bottom", {"start": v(270.33, -101.56) * mm, "end": v(306.33, -101.56) * mm});
            skLineSegment(sketch, "E100.top", {"start": v(270.33, -104.56) * mm, "end": v(306.33, -104.56) * mm});
            skLineSegment(sketch, "E100.left", {"start": v(270.33, -101.56) * mm, "end": v(270.33, -104.56) * mm});
            skLineSegment(sketch, "E100.right", {"start": v(306.33, -101.56) * mm, "end": v(306.33, -104.56) * mm});
            skLineSegment(sketch, "E101.bottom", {"start": v(331.33, 21.66) * mm, "end": v(332.33, 21.66) * mm});
            skLineSegment(sketch, "E101.top", {"start": v(331.33, -101.56) * mm, "end": v(334.33, -101.56) * mm});
            skLineSegment(sketch, "E101.right", {"start": v(334.33, 19.66) * mm, "end": v(334.33, -101.56) * mm});
            skLineSegment(sketch, "E102.bottom", {"start": v(321.33, -101.56) * mm, "end": v(334.33, -101.56) * mm});
            skLineSegment(sketch, "E102.top", {"start": v(321.33, -104.56) * mm, "end": v(334.33, -104.56) * mm});
            skLineSegment(sketch, "E102.left", {"start": v(321.33, -101.56) * mm, "end": v(321.33, -104.56) * mm});
            skLineSegment(sketch, "E102.right", {"start": v(334.33, -101.56) * mm, "end": v(334.33, -104.56) * mm});
            skLineSegment(sketch, "E103.bottom", {"start": v(210.83, 28.66) * mm, "end": v(209.83, 28.66) * mm});
            skLineSegment(sketch, "E103.top", {"start": v(210.83, 21.66) * mm, "end": v(209.83, 21.66) * mm});
            skLineSegment(sketch, "E103.left", {"start": v(210.83, 28.66) * mm, "end": v(210.83, 21.66) * mm});
            skLineSegment(sketch, "E103.right", {"start": v(209.83, 28.66) * mm, "end": v(209.83, 21.66) * mm});
            skLineSegment(sketch, "E104.bottom", {"start": v(209.83, 21.66) * mm, "end": v(203.83, 21.66) * mm});
            skLineSegment(sketch, "E104.top", {"start": v(209.83, 22.66) * mm, "end": v(203.83, 22.66) * mm});
            skLineSegment(sketch, "E104.left", {"start": v(209.83, 21.66) * mm, "end": v(209.83, 22.66) * mm});
            skLineSegment(sketch, "E104.right", {"start": v(203.83, 21.66) * mm, "end": v(203.83, 22.66) * mm});
            skLineSegment(sketch, "E105.bottom", {"start": v(270.83, 28.66) * mm, "end": v(271.83, 28.66) * mm});
            skLineSegment(sketch, "E105.top", {"start": v(270.83, 21.66) * mm, "end": v(271.83, 21.66) * mm});
            skLineSegment(sketch, "E105.left", {"start": v(270.83, 28.66) * mm, "end": v(270.83, 21.66) * mm});
            skLineSegment(sketch, "E105.right", {"start": v(271.83, 28.66) * mm, "end": v(271.83, 21.66) * mm});
            skLineSegment(sketch, "E106.bottom", {"start": v(271.83, 21.66) * mm, "end": v(277.83, 21.66) * mm});
            skLineSegment(sketch, "E106.top", {"start": v(271.83, 22.66) * mm, "end": v(277.83, 22.66) * mm});
            skLineSegment(sketch, "E106.left", {"start": v(271.83, 21.66) * mm, "end": v(271.83, 22.66) * mm});
            skLineSegment(sketch, "E106.right", {"start": v(277.83, 21.66) * mm, "end": v(277.83, 22.66) * mm});
            skPoint(sketch, "E107.visualSharp", {"position": v(147.33, 21.66) * mm});
            skArc(sketch, "E107.filletArc", {"start": v(149.33, 21.66) * mm, "mid": v(147.92, 21.07) * mm, "end": v(147.33, 19.66) * mm});
            skPoint(sketch, "E108.visualSharp", {"position": v(334.33, 21.66) * mm});
            skArc(sketch, "E108.filletArc", {"start": v(334.33, 19.66) * mm, "mid": v(333.75, 21.07) * mm, "end": v(332.33, 21.66) * mm});
            skPoint(sketch, "E109.visualSharp", {"position": v(147.33, -49.56) * mm});
            skArc(sketch, "E109.filletArc", {"start": v(147.33, -47.56) * mm, "mid": v(147.92, -48.97) * mm, "end": v(149.33, -49.56) * mm});
            skCircle(sketch, "E110", {"center": v(153.08, 13.66) * mm, "radius": 1.5 * mm, "construction": true});
            skCircle(sketch, "E111", {"center": v(153.08, -9.34) * mm, "radius": 1.5 * mm, "construction": true});
            skLineSegment(sketch, "E112.bottom", {"start": v(155.33, 16.16) * mm, "end": v(160.33, 16.16) * mm, "construction": true});
            skLineSegment(sketch, "E112.top", {"start": v(155.33, -8.84) * mm, "end": v(160.33, -8.84) * mm, "construction": true});
            skLineSegment(sketch, "E112.left", {"start": v(155.33, 16.16) * mm, "end": v(155.33, -8.84) * mm, "construction": true});
            skLineSegment(sketch, "E112.right", {"start": v(160.33, 16.16) * mm, "end": v(160.33, -8.84) * mm, "construction": true});
            skCircle(sketch, "E113", {"center": v(157.83, 11.16) * mm, "radius": 1 * mm, "construction": true});
            skPoint(sketch, "E113.centerSnap0", {"position": v(157.83, 16.16) * mm});
            skCircle(sketch, "E114", {"center": v(157.83, -3.84) * mm, "radius": 1 * mm, "construction": true});
            skCircle(sketch, "E115", {"center": v(153.08, -34.34) * mm, "radius": 1.5 * mm, "construction": true});
            skLineSegment(sketch, "E116.bottom", {"start": v(320.83, 16.16) * mm, "end": v(325.83, 16.16) * mm, "construction": true});
            skLineSegment(sketch, "E116.top", {"start": v(320.83, -8.84) * mm, "end": v(325.83, -8.84) * mm, "construction": true});
            skLineSegment(sketch, "E116.left", {"start": v(320.83, 16.16) * mm, "end": v(320.83, -8.84) * mm, "construction": true});
            skLineSegment(sketch, "E116.right", {"start": v(325.83, 16.16) * mm, "end": v(325.83, -8.84) * mm, "construction": true});
            skCircle(sketch, "E117", {"center": v(323.33, 11.16) * mm, "radius": 1 * mm});
            skPoint(sketch, "E117.centerSnap0", {"position": v(323.33, 16.16) * mm});
            skCircle(sketch, "E118", {"center": v(323.33, -3.84) * mm, "radius": 1 * mm});
            skLineSegment(sketch, "E119", {"start": v(157.98, 3.66) * mm, "end": v(328.03, 3.66) * mm, "construction": true});
            skCircle(sketch, "E120", {"center": v(234.33, -60.84) * mm, "radius": 12.5 * mm, "construction": true});
            skLineSegment(sketch, "E121", {"start": v(268.33, -87.06) * mm, "end": v(268.33, -87.06) * mm});
            skCircle(sketch, "E122", {"center": v(196.58, -23.34) * mm, "radius": 8 * mm});
            skCircle(sketch, "E123", {"center": v(168.08, -28.34) * mm, "radius": 4 * mm});
            skCircle(sketch, "E124", {"center": v(224.08, -23.34) * mm, "radius": 8 * mm});
            skCircle(sketch, "E125", {"center": v(256.58, -23.34) * mm, "radius": 8 * mm});
            skCircle(sketch, "E126", {"center": v(284.08, -23.34) * mm, "radius": 8 * mm});
            skCircle(sketch, "E127", {"center": v(312.58, -23.34) * mm, "radius": 8 * mm});
            skCircle(sketch, "E128", {"center": v(268.33, -71.06) * mm, "radius": 8 * mm, "construction": true});
            skPoint(sketch, "E128.centerSnap0", {"position": v(268.33, -42.56) * mm});
            skPoint(sketch, "E129.visualSharp", {"position": v(258.33, -87.06) * mm});
            skArc(sketch, "E129.filletArc", {"start": v(258.33, -77.06) * mm, "mid": v(261.26, -84.13) * mm, "end": v(268.33, -87.06) * mm});
            skPoint(sketch, "E130.visualSharp", {"position": v(278.33, -87.06) * mm});
            skArc(sketch, "E130.filletArc", {"start": v(268.33, -87.06) * mm, "mid": v(275.4, -84.13) * mm, "end": v(278.33, -77.06) * mm});
            skSolve(sketch);
        }
        {
            var Q0;
            Q0=makeQuery(id+"F19.imprint","IMPRINT",FACE,{"disambiguationData":[TD([[makeQuery(id+"F19.imprint","IMPRINT",EDGE,{"derivedFrom":sQuery(id+"F19.wireOp",EDGE,"E82")}),1.0]])]});
            var Q1;
            Q1=makeQuery(id+"F19.imprint","IMPRINT",FACE,{"disambiguationData":[TD([[makeQuery(id+"F19.imprint","IMPRINT",EDGE,{"derivedFrom":sQuery(id+"F19.wireOp",EDGE,"E83")}),1.0]])]});
            var Q2;
            Q2=makeQuery(id+"F19.imprint","IMPRINT",FACE,{"disambiguationData":[TD([[makeQuery(id+"F19.imprint","IMPRINT",EDGE,{"derivedFrom":sQuery(id+"F19.wireOp",EDGE,"E84")}),1.0]])]});
            var Q3;
            Q3=makeQuery(id+"F19.imprint","IMPRINT",FACE,{"disambiguationData":[TD([[makeQuery(id+"F19.imprint","IMPRINT",EDGE,{"derivedFrom":sQuery(id+"F19.wireOp",EDGE,"E86")}),1.0]])]});
            var Q4;
            Q4=makeQuery(id+"F19.imprint","IMPRINT",FACE,{"disambiguationData":[TD([[makeQuery(id+"F19.imprint","IMPRINT",EDGE,{"derivedFrom":sQuery(id+"F19.wireOp",EDGE,"E87")}),1.0]])]});
            var Q5;
            Q5=makeQuery(id+"F19.imprint","IMPRINT",FACE,{"disambiguationData":[TD([[makeQuery(id+"F19.imprint","IMPRINT",EDGE,{"derivedFrom":sQuery(id+"F19.wireOp",EDGE,"E88")}),1.0]])]});
            var Q6;
            Q6=makeQuery(id+"F19.imprint","IMPRINT",FACE,{"disambiguationData":[TD([[makeQuery(id+"F19.imprint","IMPRINT",EDGE,{"derivedFrom":sQuery(id+"F19.wireOp",EDGE,"182ebfe6-2736-47e7-aa4b-23692cbbae48")}),1.0]])]});
            var Q7;
            Q7=makeQuery(id+"F19.imprint","IMPRINT",FACE,{"disambiguationData":[TD([[makeQuery(id+"F19.imprint","IMPRINT",EDGE,{"derivedFrom":sQuery(id+"F19.wireOp",EDGE,"e7df0eac-41cd-404f-bdd1-8c65fee716b7")}),1.0]])]});
            var Q8;
            Q8=makeQuery(id+"F19.imprint","IMPRINT",FACE,{"disambiguationData":[TD([[makeQuery(id+"F19.imprint","IMPRINT",EDGE,{"derivedFrom":sQuery(id+"F19.wireOp",EDGE,"6b2fa6bf-2d88-4192-aa23-f9972aa437f7")}),1.0]])]});
            var Q9;
            Q9=makeQuery(id+"F19.imprint","IMPRINT",FACE,{"disambiguationData":[TD([[makeQuery(id+"F19.imprint","IMPRINT",EDGE,{"derivedFrom":sQuery(id+"F19.wireOp",EDGE,"76bc2124-5548-41a5-9276-e67c2ab8353c")}),1.0]])]});
            var Q10;
            Q10=makeQuery(id+"F19.imprint","IMPRINT",FACE,{"disambiguationData":[TD([[makeQuery(id+"F19.imprint","IMPRINT",EDGE,{"derivedFrom":sQuery(id+"F19.wireOp",EDGE,"525520f9-84c5-4c3a-afae-55c33ce15ad5")}),1.0]])]});
            var Q11;
            Q11=makeQuery(id+"F19.imprint","IMPRINT",FACE,{"disambiguationData":[TD([[makeQuery(id+"F19.imprint","IMPRINT",EDGE,{"derivedFrom":sQuery(id+"F19.wireOp",EDGE,"E92.left")}),1.0]])]});
            var Q12;
            Q12=makeQuery(id+"F19.imprint","IMPRINT",FACE,{"disambiguationData":[TD([[makeQuery(id+"F19.imprint","IMPRINT",EDGE,{"derivedFrom":sQuery(id+"F19.wireOp",EDGE,"E89")}),1.0]])]});
            var Q13;
            Q13=makeQuery(id+"F19.imprint","IMPRINT",FACE,{"disambiguationData":[TD([[makeQuery(id+"F19.imprint","IMPRINT",EDGE,{"derivedFrom":sQuery(id+"F19.wireOp",EDGE,"E90")}),1.0]])]});
            var Q14;
            Q14=makeQuery(id+"F19.imprint","IMPRINT",FACE,{"disambiguationData":[TD([[makeQuery(id+"F19.imprint","IMPRINT",EDGE,{"derivedFrom":sQuery(id+"F19.wireOp",EDGE,"E85")}),1.0]])]});
            var Q15;
            Q15=makeQuery(id+"F19.imprint","IMPRINT",FACE,{"disambiguationData":[TD([[makeQuery(id+"F19.imprint","IMPRINT",EDGE,{"derivedFrom":sQuery(id+"F19.wireOp",EDGE,"E95")}),1.0]])]});
            var Q16;
            Q16=makeQuery(id+"F19.imprint","IMPRINT",FACE,{"disambiguationData":[TD([[makeQuery(id+"F19.imprint","IMPRINT",EDGE,{"derivedFrom":sQuery(id+"F19.wireOp",EDGE,"OKDoaGtq-tjQu-zaJd-eQLP-X6xpVMhiND1Y")}),1.0]])]});
            var Q17;
            Q17=makeQuery(id+"F19.imprint","IMPRINT",FACE,{"disambiguationData":[TD([[makeQuery(id+"F19.imprint","IMPRINT",EDGE,{"derivedFrom":sQuery(id+"F19.wireOp",EDGE,"E94")}),1.0]])]});
            var Q18;
            Q18=makeQuery(id+"F19.imprint","IMPRINT",FACE,{"disambiguationData":[TD([[makeQuery(id+"F19.imprint","IMPRINT",EDGE,{"derivedFrom":sQuery(id+"F19.wireOp",EDGE,"E123")}),1.0]])]});
            var Q19;
            Q19=makeQuery(id+"F19.imprint","IMPRINT",FACE,{"disambiguationData":[TD([[makeQuery(id+"F19.imprint","IMPRINT",EDGE,{"derivedFrom":sQuery(id+"F19.wireOp",EDGE,"E122")}),1.0]])]});
            var Q20;
            Q20=makeQuery(id+"F19.imprint","IMPRINT",FACE,{"disambiguationData":[TD([[makeQuery(id+"F19.imprint","IMPRINT",EDGE,{"derivedFrom":sQuery(id+"F19.wireOp",EDGE,"E124")}),1.0]])]});
            var Q21;
            Q21=makeQuery(id+"F19.imprint","IMPRINT",FACE,{"disambiguationData":[TD([[makeQuery(id+"F19.imprint","IMPRINT",EDGE,{"derivedFrom":sQuery(id+"F19.wireOp",EDGE,"E125")}),1.0]])]});
            var Q22;
            Q22=makeQuery(id+"F19.imprint","IMPRINT",FACE,{"disambiguationData":[TD([[makeQuery(id+"F19.imprint","IMPRINT",EDGE,{"derivedFrom":sQuery(id+"F19.wireOp",EDGE,"E126")}),1.0]])]});
            var Q23;
            Q23=makeQuery(id+"F19.imprint","IMPRINT",FACE,{"disambiguationData":[TD([[makeQuery(id+"F19.imprint","IMPRINT",EDGE,{"derivedFrom":sQuery(id+"F19.wireOp",EDGE,"E127")}),1.0]])]});
            extrude(context, id + "F20", {"entities" : qUnion([Q0, Q1, Q2, Q3, Q4, Q5, Q6, Q7, Q8, Q9, Q10, Q11, Q12, Q13, Q14, Q15, Q16, Q17, Q18, Q19, Q20, Q21, Q22, Q23]), "operationType" : NewBodyOperationType.REMOVE, "oppositeDirection" : true, "depth" : 5 * mm});
        }
        {
            var Q0;
            Q0=qCreatedBy(makeId("Top.planeOp"),FACE);
            var sketch = newSketch(context, id + "F21", { "sketchPlane" : qUnion([Q0])});
            skLineSegment(sketch, "E131.bottom", {"start": v(87.15, 21.4) * mm, "end": v(104.65, 21.4) * mm});
            skLineSegment(sketch, "E131.top", {"start": v(87.15, -48.87) * mm, "end": v(104.65, -48.87) * mm});
            skLineSegment(sketch, "E131.left", {"start": v(87.15, 21.4) * mm, "end": v(87.15, -48.87) * mm});
            skLineSegment(sketch, "E131.right", {"start": v(104.65, 21.4) * mm, "end": v(104.65, -48.87) * mm});
            skCircle(sketch, "E132", {"center": v(102.15, 16.4) * mm, "radius": 1 * mm, "construction": true});
            skCircle(sketch, "E133", {"center": v(102.65, 13.4) * mm, "radius": 1.1 * mm});
            skCircle(sketch, "E134", {"center": v(102.65, -9.6) * mm, "radius": 1.1 * mm});
            skCircle(sketch, "E135", {"center": v(102.65, -34.6) * mm, "radius": 1.1 * mm});
            skCircle(sketch, "E136", {"center": v(90.9, 9.4) * mm, "radius": 1.5 * mm});
            skCircle(sketch, "E137", {"center": v(90.9, -38.87) * mm, "radius": 1.5 * mm});
            skCircle(sketch, "E138", {"center": v(90.9, 9.4) * mm, "radius": 3.25 * mm, "construction": true});
            skSolve(sketch);
        }
        {
            var Q0;
            Q0=makeQuery(id+"F21.imprint","IMPRINT",FACE,{"disambiguationData":[TD([[makeQuery(id+"F21.imprint","IMPRINT",EDGE,{"derivedFrom":sQuery(id+"F21.wireOp",EDGE,"E131.bottom")}),-1.0]])]});
            extrude(context, id + "F22", {"entities" : qUnion([Q0]), "depth" : 1 * mm});
        }
        {
            var Q0;
            Q0=qCreatedBy(makeId("Top.planeOp"),FACE);
            var sketch = newSketch(context, id + "F23", { "sketchPlane" : qUnion([Q0])});
            skLineSegment(sketch, "E139.bottom", {"start": v(370, 20.23) * mm, "end": v(387.5, 20.23) * mm});
            skLineSegment(sketch, "E139.top", {"start": v(370, -107.8) * mm, "end": v(387.5, -107.8) * mm});
            skLineSegment(sketch, "E139.left", {"start": v(370, 20.23) * mm, "end": v(370, -107.8) * mm});
            skLineSegment(sketch, "E139.right", {"start": v(387.5, 20.23) * mm, "end": v(387.5, -107.8) * mm});
            skCircle(sketch, "E140", {"center": v(372, 12.23) * mm, "radius": 1.1 * mm});
            skCircle(sketch, "E141", {"center": v(372, -7.77) * mm, "radius": 1.1 * mm});
            skCircle(sketch, "E142", {"center": v(372, -27.77) * mm, "radius": 1.1 * mm});
            skCircle(sketch, "E143", {"center": v(372, -47.77) * mm, "radius": 1.1 * mm});
            skCircle(sketch, "E144", {"center": v(372, -67.77) * mm, "radius": 1.1 * mm});
            skCircle(sketch, "E145", {"center": v(372, -87.77) * mm, "radius": 1.1 * mm});
            skCircle(sketch, "E146", {"center": v(383.74, 8.23) * mm, "radius": 1.5 * mm});
            skCircle(sketch, "E147", {"center": v(383.74, -43.77) * mm, "radius": 1.5 * mm});
            skCircle(sketch, "E148", {"center": v(383.74, -95.8) * mm, "radius": 1.5 * mm});
            skSolve(sketch);
        }
        {
            var Q0;
            Q0=makeQuery(id+"F23.imprint","IMPRINT",FACE,{"disambiguationData":[TD([[makeQuery(id+"F23.imprint","IMPRINT",EDGE,{"derivedFrom":sQuery(id+"F23.wireOp",EDGE,"E139.bottom")}),-1.0]])]});
            extrude(context, id + "F24", {"entities" : qUnion([Q0]), "depth" : 1 * mm});
        }
        {
            var Q0;
            Q0=makeQuery(id+"F19.imprint","IMPRINT",FACE,{"disambiguationData":[TD([[makeQuery(id+"F19.imprint","IMPRINT",EDGE,{"derivedFrom":sQuery(id+"F19.wireOp",EDGE,"E91.top")}),1.0]])]});
            var sketch = newSketch(context, id + "F25", { "sketchPlane" : qUnion([Q0])});
            skLineSegment(sketch, "E149.bottom", {"start": v(150.36, 18.45) * mm, "end": v(329.5, 18.45) * mm});
            skLineSegment(sketch, "E149.top", {"start": v(178.72, -100.9) * mm, "end": v(329.5, -100.9) * mm});
            skLineSegment(sketch, "E149.left", {"start": v(150.36, 18.45) * mm, "end": v(150.36, -49.22) * mm});
            skLineSegment(sketch, "E149.right", {"start": v(329.5, 18.45) * mm, "end": v(329.5, -100.9) * mm});
            skLineSegment(sketch, "E150", {"start": v(150.36, -49.22) * mm, "end": v(178.72, -49.22) * mm});
            skLineSegment(sketch, "E151", {"start": v(178.72, -49.22) * mm, "end": v(178.72, -100.9) * mm});
            skLineSegment(sketch, "E152.bottom", {"start": v(8.56, -7.76) * mm, "end": v(28.56, -7.76) * mm});
            skLineSegment(sketch, "E152.top", {"start": v(8.56, -27.76) * mm, "end": v(28.56, -27.76) * mm});
            skLineSegment(sketch, "E152.left", {"start": v(8.56, -7.76) * mm, "end": v(8.56, -27.76) * mm});
            skLineSegment(sketch, "E152.right", {"start": v(28.56, -7.76) * mm, "end": v(28.56, -27.76) * mm});
            skCircle(sketch, "E153", {"center": v(18.56, -17.76) * mm, "radius": 7.5 * mm});
            skPoint(sketch, "E153.centerSnap0", {"position": v(8.56, -17.76) * mm});
            skPoint(sketch, "E153.centerSnap1", {"position": v(18.56, -7.76) * mm});
            skLineSegment(sketch, "E154.left", {"start": v(-58.94, -27.5) * mm, "end": v(-58.94, -58.75) * mm});
            skLineSegment(sketch, "E154.right", {"start": v(-39.94, -27.5) * mm, "end": v(-39.94, -58.75) * mm});
            skArc(sketch, "E155", {"start": v(-58.94, -58.75) * mm, "mid": v(-49.44, -68.25) * mm, "end": v(-39.94, -58.75) * mm});
            skLineSegment(sketch, "E156", {"start": v(-58.94, -27.5) * mm, "end": v(-39.94, -27.5) * mm});
            skLineSegment(sketch, "E157.bottom", {"start": v(-61.94, -24.5) * mm, "end": v(-36.94, -24.5) * mm});
            skLineSegment(sketch, "E157.top", {"start": v(-61.94, -71.25) * mm, "end": v(-36.94, -71.25) * mm});
            skLineSegment(sketch, "E157.left", {"start": v(-61.94, -24.5) * mm, "end": v(-61.94, -71.25) * mm});
            skLineSegment(sketch, "E157.right", {"start": v(-36.94, -24.5) * mm, "end": v(-36.94, -71.25) * mm});
            skSolve(sketch);
        }
        {
            var Q0;
            Q0=makeQuery(id+"F25.imprint","IMPRINT",FACE,{"disambiguationData":[TD([[makeQuery(id+"F25.imprint","IMPRINT",EDGE,{"derivedFrom":sQuery(id+"F25.wireOp",EDGE,"E152.bottom")}),-1.0]])]});
            var Q1;
            Q1=makeQuery(id+"F25.imprint","IMPRINT",FACE,{"disambiguationData":[TD([[makeQuery(id+"F25.imprint","IMPRINT",EDGE,{"derivedFrom":sQuery(id+"F25.wireOp",EDGE,"E154.left")}),-1.0]])]});
            extrude(context, id + "F26", {"entities" : qUnion([Q0, Q1]), "depth" : 2 * mm});
        }
        {
            var Q0;
            Q0=makeQuery(id+"F24.opExtrude","SWEPT_FACE",FACE,{"disambiguationData":[OSD([sQuery(id+"F23.wireOp",EDGE,"E139.left")])]});
            extrude(context, id + "F27", {"entities" : qUnion([Q0]), "operationType" : NewBodyOperationType.ADD, "depth" : 1 * mm});
        }
        {
            var Q0;
            Q0=makeQuery(id+"F22.opExtrude","SWEPT_FACE",FACE,{"disambiguationData":[OSD([sQuery(id+"F21.wireOp",EDGE,"E131.right")])]});
            extrude(context, id + "F28", {"entities" : qUnion([Q0]), "operationType" : NewBodyOperationType.ADD, "depth" : 1 * mm});
        }
        {
            var Q0;
            Q0=makeQuery(id+"F24.opExtrude","SWEPT_EDGE",EDGE,{"disambiguationData":[OSD([sQuery(id+"F23.wireOp",EDGE,"E139.bottom"),sQuery(id+"F23.wireOp",EDGE,"E139.right")])]});
            var Q1;
            Q1=makeQuery(id+"F27.opExtrude","CAP_EDGE",EDGE,{"disambiguationData":[OSD([sQuery(id+"F23.wireOp",EDGE,"E139.bottom"),sQuery(id+"F23.wireOp",EDGE,"E139.left")])],"isStart":false});
            var Q2;
            Q2=makeQuery(id+"F24.opExtrude","SWEPT_EDGE",EDGE,{"disambiguationData":[OSD([sQuery(id+"F23.wireOp",EDGE,"E139.top"),sQuery(id+"F23.wireOp",EDGE,"E139.right")])]});
            var Q3;
            Q3=makeQuery(id+"F27.opExtrude","CAP_EDGE",EDGE,{"disambiguationData":[OSD([sQuery(id+"F23.wireOp",EDGE,"E139.top"),sQuery(id+"F23.wireOp",EDGE,"E139.left")])],"isStart":false});
            var Q4;
            Q4=makeQuery(id+"F28.opExtrude","CAP_EDGE",EDGE,{"disambiguationData":[OSD([sQuery(id+"F21.wireOp",EDGE,"E131.top"),sQuery(id+"F21.wireOp",EDGE,"E131.right")])],"isStart":false});
            var Q5;
            Q5=makeQuery(id+"F22.opExtrude","SWEPT_EDGE",EDGE,{"disambiguationData":[OSD([sQuery(id+"F21.wireOp",EDGE,"E131.top"),sQuery(id+"F21.wireOp",EDGE,"E131.left")])]});
            var Q6;
            Q6=makeQuery(id+"F28.opExtrude","CAP_EDGE",EDGE,{"disambiguationData":[OSD([sQuery(id+"F21.wireOp",EDGE,"E131.bottom"),sQuery(id+"F21.wireOp",EDGE,"E131.right")])],"isStart":false});
            var Q7;
            Q7=makeQuery(id+"F22.opExtrude","SWEPT_EDGE",EDGE,{"disambiguationData":[OSD([sQuery(id+"F21.wireOp",EDGE,"E131.bottom"),sQuery(id+"F21.wireOp",EDGE,"E131.left")])]});
            fillet(context, id + "F29", {"entities" : qUnion([Q0, Q1, Q2, Q3, Q4, Q5, Q6, Q7]), "radius" : 2 * mm, "tangentPropagation" : true, "allowEdgeOverflow" : false});
        }
        {
            var Q0;
            Q0=qCreatedBy(makeId("Top.planeOp"),FACE);
            var sketch = newSketch(context, id + "F30", { "sketchPlane" : qUnion([Q0])});
            skCircle(sketch, "E158", {"center": v(29.82, -55.72) * mm, "radius": 3.25 * mm});
            skCircle(sketch, "E159", {"center": v(50.26, -57.48) * mm, "radius": 8 * mm});
            skSolve(sketch);
        }
        {
            var Q0;
            Q0=makeQuery(id+"F30.imprint","IMPRINT",FACE,{"disambiguationData":[TD([[makeQuery(id+"F30.imprint","IMPRINT",EDGE,{"derivedFrom":sQuery(id+"F30.wireOp",EDGE,"E158")}),1.0]])]});
            extrude(context, id + "F31", {"entities" : qUnion([Q0]), "depth" : 25 * mm});
        }
        {
            var Q0;
            Q0=makeQuery(id+"F30.imprint","IMPRINT",FACE,{"disambiguationData":[TD([[makeQuery(id+"F30.imprint","IMPRINT",EDGE,{"derivedFrom":sQuery(id+"F30.wireOp",EDGE,"E159")}),1.0]])]});
            extrude(context, id + "F32", {"entities" : qUnion([Q0]), "depth" : 6.5 * mm});
        }
    });
